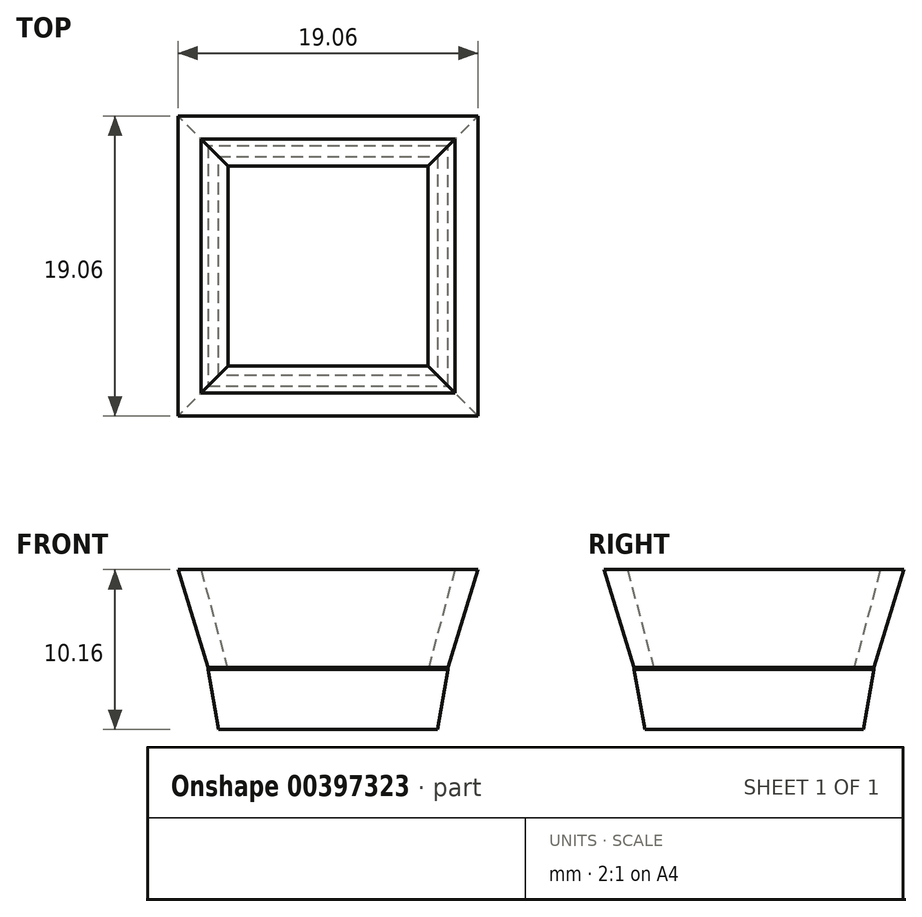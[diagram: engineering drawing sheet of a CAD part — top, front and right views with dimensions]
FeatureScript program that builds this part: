
annotation { "Feature Type Name" : "Feature", "Feature Type Description" : "" }
export const myFeature = defineFeature(function(context is Context, id is Id, definition is map)
    precondition{}
    {
        {
            var Q0;
            Q0=qCreatedBy(makeId("Top.planeOp"),FACE);
            var sketch = newSketch(context, id + "F0", { "sketchPlane" : qUnion([Q0])});
            skLineSegment(sketch, "E0.bottom", {"start": v(9.53, 9.53) * mm, "end": v(-9.52, 9.53) * mm});
            skLineSegment(sketch, "E0.top", {"start": v(9.52, -9.53) * mm, "end": v(-9.53, -9.53) * mm});
            skLineSegment(sketch, "E0.left", {"start": v(9.53, 9.53) * mm, "end": v(9.52, -9.53) * mm});
            skLineSegment(sketch, "E0.right", {"start": v(-9.52, 9.53) * mm, "end": v(-9.53, -9.53) * mm});
            skPoint(sketch, "E0.middle", {"position": v(0, 0) * mm});
            skLineSegment(sketch, "E1.bottom", {"start": v(-6.35, 6.35) * mm, "end": v(6.35, 6.35) * mm});
            skLineSegment(sketch, "E1.top", {"start": v(-6.35, -6.35) * mm, "end": v(6.35, -6.35) * mm});
            skLineSegment(sketch, "E1.left", {"start": v(-6.35, 6.35) * mm, "end": v(-6.35, -6.35) * mm});
            skLineSegment(sketch, "E1.right", {"start": v(6.35, 6.35) * mm, "end": v(6.35, -6.35) * mm});
            skSolve(sketch);
        }
        {
            var Q0;
            Q0=makeQuery(id+"F0.imprint","IMPRINT",FACE,{"disambiguationData":[TD([[makeQuery(id+"F0.imprint","IMPRINT",EDGE,{"derivedFrom":sQuery(id+"F0.wireOp",EDGE,"E0.bottom")}),1.0]])]});
            extrude(context, id + "F1", {"entities" : qUnion([Q0]), "depth" : 6.35 * mm});
        }
        {
            var Q0;
            Q0=qCreatedBy(makeId("Top.planeOp"),FACE);
            var sketch = newSketch(context, id + "F2", { "sketchPlane" : qUnion([Q0])});
            skLineSegment(sketch, "E2.bottom", {"start": v(-7.62, 7.62) * mm, "end": v(7.62, 7.62) * mm});
            skLineSegment(sketch, "E2.top", {"start": v(-7.62, -7.62) * mm, "end": v(7.62, -7.62) * mm});
            skLineSegment(sketch, "E2.left", {"start": v(-7.62, 7.62) * mm, "end": v(-7.62, -7.62) * mm});
            skLineSegment(sketch, "E2.right", {"start": v(7.62, 7.62) * mm, "end": v(7.62, -7.62) * mm});
            skPoint(sketch, "E2.middle", {"position": v(0, 0) * mm});
            skSolve(sketch);
        }
        {
            var Q0;
            Q0 = qSketchRegion(id + "F2", true);
            extrude(context, id + "F3", {"entities" : qUnion([Q0]), "operationType" : NewBodyOperationType.ADD, "oppositeDirection" : true, "depth" : 3.8 * mm});
        }
        {
            var Q0;
            Q0=makeQuery(id+"F1.opExtrude","CAP_EDGE",EDGE,{"disambiguationData":[OSD([sQuery(id+"F0.wireOp",EDGE,"E1.bottom")])],"isStart":false});
            var Q1;
            Q1=makeQuery(id+"F1.opExtrude","CAP_EDGE",EDGE,{"disambiguationData":[OSD([sQuery(id+"F0.wireOp",EDGE,"E1.right")])],"isStart":false});
            var Q2;
            Q2=makeQuery(id+"F1.opExtrude","CAP_EDGE",EDGE,{"disambiguationData":[OSD([sQuery(id+"F0.wireOp",EDGE,"E1.top")])],"isStart":false});
            var Q3;
            Q3=makeQuery(id+"F1.opExtrude","CAP_EDGE",EDGE,{"disambiguationData":[OSD([sQuery(id+"F0.wireOp",EDGE,"E1.left")])],"isStart":false});
            chamfer(context, id + "F4", {"entities" : qUnion([Q0, Q1, Q2, Q3]), "chamferType" : ChamferType.OFFSET_ANGLE, "width" : 6.35 * mm, "oppositeDirection" : true, "angle" : 15 * degree, "tangentPropagation" : true});
        }
        {
            var Q0;
            Q0=makeQuery(id+"F1.opExtrude","CAP_EDGE",EDGE,{"disambiguationData":[OSD([sQuery(id+"F0.wireOp",EDGE,"E0.bottom")])],"isStart":true});
            var Q1;
            Q1=makeQuery(id+"F1.opExtrude","CAP_EDGE",EDGE,{"disambiguationData":[OSD([sQuery(id+"F0.wireOp",EDGE,"E0.left")])],"isStart":true});
            var Q2;
            Q2=makeQuery(id+"F1.opExtrude","CAP_EDGE",EDGE,{"disambiguationData":[OSD([sQuery(id+"F0.wireOp",EDGE,"E0.top")])],"isStart":true});
            var Q3;
            Q3=makeQuery(id+"F1.opExtrude","CAP_EDGE",EDGE,{"disambiguationData":[OSD([sQuery(id+"F0.wireOp",EDGE,"E0.right")])],"isStart":true});
            chamfer(context, id + "F5", {"entities" : qUnion([Q0, Q1, Q2, Q3]), "chamferType" : ChamferType.OFFSET_ANGLE, "width" : 6.35 * mm, "oppositeDirection" : false, "angle" : 17 * degree, "tangentPropagation" : true});
        }
        {
            var Q0;
            Q0=makeQuery(id+"F3.opExtrude","CAP_EDGE",EDGE,{"disambiguationData":[OSD([sQuery(id+"F2.wireOp",EDGE,"E2.right")])],"isStart":false});
            var Q1;
            Q1=makeQuery(id+"F3.opExtrude","CAP_EDGE",EDGE,{"disambiguationData":[OSD([sQuery(id+"F2.wireOp",EDGE,"E2.top")])],"isStart":false});
            var Q2;
            Q2=makeQuery(id+"F3.opExtrude","CAP_EDGE",EDGE,{"disambiguationData":[OSD([sQuery(id+"F2.wireOp",EDGE,"E2.left")])],"isStart":false});
            var Q3;
            Q3=makeQuery(id+"F3.opExtrude","CAP_EDGE",EDGE,{"disambiguationData":[OSD([sQuery(id+"F2.wireOp",EDGE,"E2.bottom")])],"isStart":false});
            chamfer(context, id + "F6", {"entities" : qUnion([Q0, Q1, Q2, Q3]), "chamferType" : ChamferType.OFFSET_ANGLE, "width" : 3.8 * mm, "oppositeDirection" : true, "angle" : 10 * degree, "tangentPropagation" : true});
        }
    });
